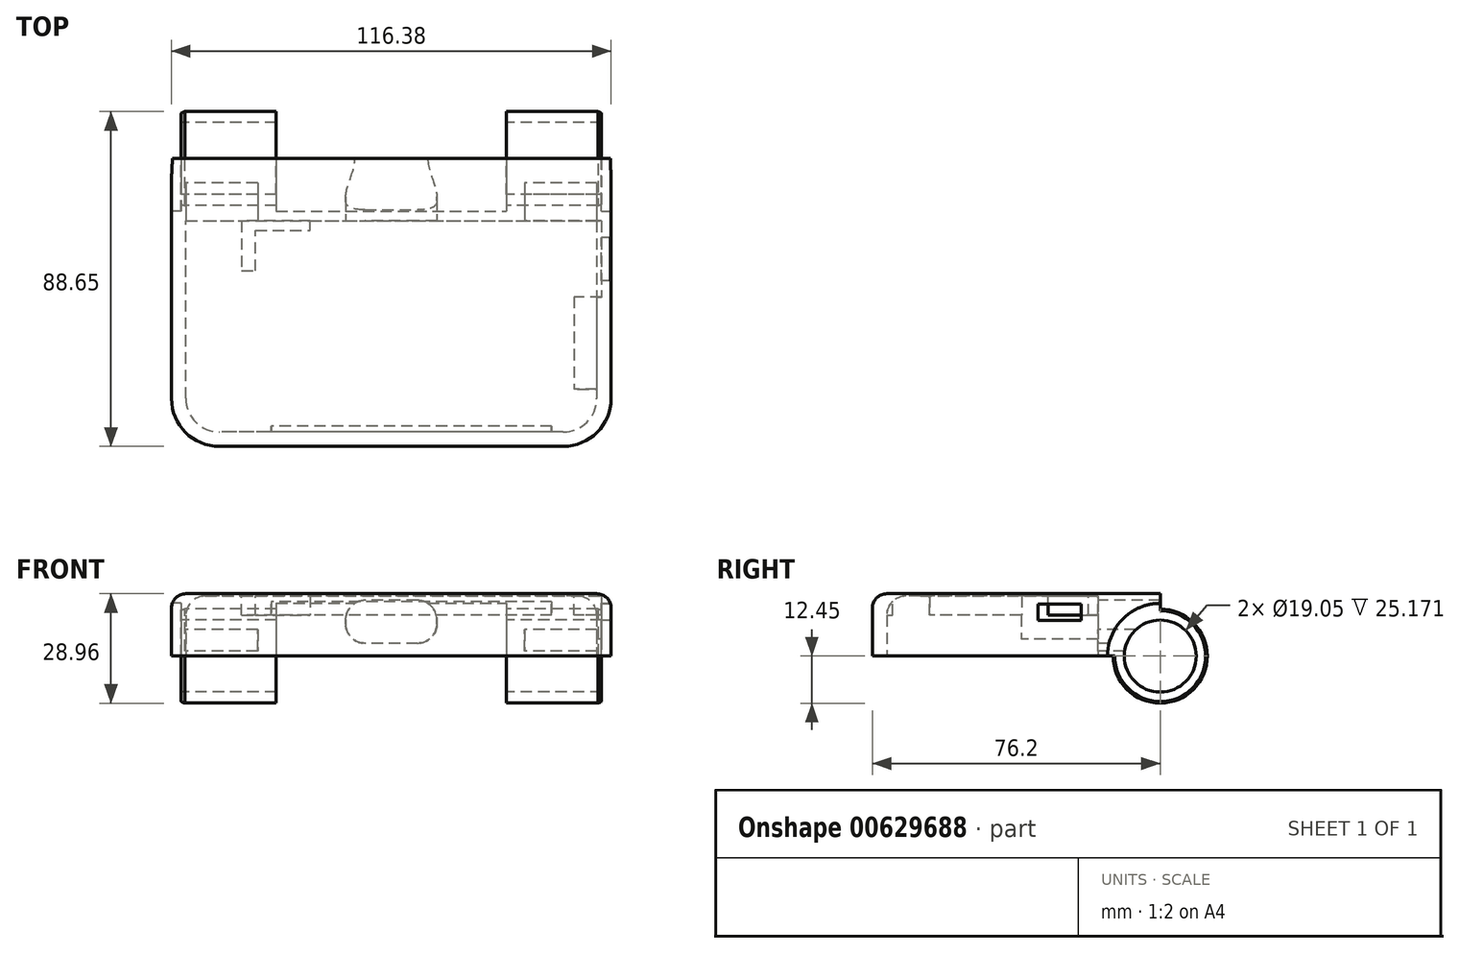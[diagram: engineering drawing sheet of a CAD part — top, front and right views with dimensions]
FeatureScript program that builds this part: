
annotation { "Feature Type Name" : "Feature", "Feature Type Description" : "" }
export const myFeature = defineFeature(function(context is Context, id is Id, definition is map)
    precondition{}
    {
        {
            var Q0;
            Q0=qCreatedBy(makeId("Top.planeOp"),FACE);
            var sketch = newSketch(context, id + "F0", { "sketchPlane" : qUnion([Q0])});
            skLineSegment(sketch, "E0.bottom", {"start": v(58.2, 38.1) * mm, "end": v(-58.2, 38.1) * mm});
            skLineSegment(sketch, "E0.top", {"start": v(58.2, -38.1) * mm, "end": v(-58.2, -38.1) * mm});
            skLineSegment(sketch, "E0.left", {"start": v(58.2, 38.1) * mm, "end": v(58.2, -38.1) * mm});
            skLineSegment(sketch, "E0.right", {"start": v(-58.2, 38.1) * mm, "end": v(-58.2, -38.1) * mm});
            skPoint(sketch, "E0.middle", {"position": v(0, 0) * mm});
            skSolve(sketch);
        }
        {
            var Q0;
            Q0 = qSketchRegion(id + "F0", true);
            extrude(context, id + "F1", {"entities" : qUnion([Q0]), "depth" : 16.5 * mm, "offsetDistance" : 25.4 * mm});
        }
        {
            var Q0;
            Q0=qCreatedBy(makeId("Right.planeOp"),FACE);
            var sketch = newSketch(context, id + "F2", { "sketchPlane" : qUnion([Q0])});
            skCircle(sketch, "E1", {"center": v(38.1, 0) * mm, "radius": 12.7 * mm});
            skSolve(sketch);
        }
        {
            var Q0;
            Q0 = qSketchRegion(id + "F2", true);
            extrude(context, id + "F3", {"entities" : qUnion([Q0]), "operationType" : NewBodyOperationType.ADD, "endBound" : BoundingType.SYMMETRIC, "depth" : 116.38 * mm, "offsetDistance" : 25.4 * mm});
        }
        {
            var Q0;
            Q0=makeQuery(id+"F1.opExtrude","SWEPT_EDGE",EDGE,{"disambiguationData":[OSD([sQuery(id+"F0.wireOp",EDGE,"E0.top"),sQuery(id+"F0.wireOp",EDGE,"E0.right")])]});
            var Q1;
            Q1=makeQuery(id+"F1.opExtrude","SWEPT_EDGE",EDGE,{"disambiguationData":[OSD([sQuery(id+"F0.wireOp",EDGE,"E0.top"),sQuery(id+"F0.wireOp",EDGE,"E0.left")])]});
            fillet(context, id + "F4", {"entities" : qUnion([Q0, Q1]), "radius" : 12.7 * mm, "tangentPropagation" : true, "allowEdgeOverflow" : false});
        }
        {
            var Q0;
            Q0=makeQuery(id+"F1.opExtrude","CAP_FACE",FACE,{"disambiguationData":[OSD([sQuery(id+"F0.wireOp",EDGE,"E0.bottom"),sQuery(id+"F0.wireOp",EDGE,"E0.top"),sQuery(id+"F0.wireOp",EDGE,"E0.left"),sQuery(id+"F0.wireOp",EDGE,"E0.right")])],"isStart":true});
            var sketch = newSketch(context, id + "F5", { "sketchPlane" : qUnion([Q0])});
            skLineSegment(sketch, "E2.0", {"start": v(-54.38, -21.6) * mm, "end": v(54.38, -21.6) * mm});
            skArc(sketch, "E2.1", {"start": v(54.38, 25.4) * mm, "mid": v(51.78, 31.69) * mm, "end": v(45.5, 34.29) * mm});
            skLineSegment(sketch, "E2.2", {"start": v(45.5, 34.3) * mm, "end": v(-45.5, 34.3) * mm});
            skLineSegment(sketch, "E2.3", {"start": v(54.38, -21.6) * mm, "end": v(54.38, 25.4) * mm});
            skArc(sketch, "E2.4", {"start": v(-45.5, 34.3) * mm, "mid": v(-51.78, 31.69) * mm, "end": v(-54.38, 25.4) * mm});
            skLineSegment(sketch, "E2.5", {"start": v(-54.38, 25.4) * mm, "end": v(-54.38, -21.6) * mm});
            skSolve(sketch);
        }
        {
            var Q0;
            Q0 = qSketchRegion(id + "F5", true);
            extrude(context, id + "F6", {"entities" : qUnion([Q0]), "operationType" : NewBodyOperationType.REMOVE, "oppositeDirection" : true, "depth" : 15.88 * mm, "offsetDistance" : 25.4 * mm});
        }
        {
            var Q0;
            Q0=qCreatedBy(makeId("Right.planeOp"),FACE);
            var sketch = newSketch(context, id + "F7", { "sketchPlane" : qUnion([Q0])});
            skCircle(sketch, "E3", {"center": v(38.1, 0) * mm, "radius": 6.99 * mm});
            skSolve(sketch);
        }
        {
            var Q0;
            Q0=qCreatedBy(makeId("Top.planeOp"),FACE);
            var sketch = newSketch(context, id + "F8", { "sketchPlane" : qUnion([Q0])});
            skLineSegment(sketch, "E4", {"start": v(0, 25.4) * mm, "end": v(-30.48, 25.4) * mm, "construction": true});
            skLineSegment(sketch, "E5", {"start": v(-30.48, 25.4) * mm, "end": v(-30.48, 28.58) * mm});
            skLineSegment(sketch, "E6", {"start": v(-30.48, 28.58) * mm, "end": v(-24.13, 28.58) * mm});
            skLineSegment(sketch, "E7", {"start": v(-24.13, 28.58) * mm, "end": v(-24.13, 28.58) * mm});
            skLineSegment(sketch, "E8", {"start": v(-24.13, 28.58) * mm, "end": v(-19.05, 28.58) * mm});
            skLineSegment(sketch, "E9", {"start": v(-19.05, 28.57) * mm, "end": v(-19.05, 38.1) * mm});
            skLineSegment(sketch, "E10", {"start": v(-19.05, 38.1) * mm, "end": v(0, 38.1) * mm});
            skLineSegment(sketch, "E11", {"start": v(0, 38.1) * mm, "end": v(19.05, 38.1) * mm});
            skLineSegment(sketch, "E12", {"start": v(19.05, 38.1) * mm, "end": v(19.05, 28.57) * mm});
            skLineSegment(sketch, "E13", {"start": v(19.05, 28.57) * mm, "end": v(24.13, 28.58) * mm});
            skLineSegment(sketch, "E14", {"start": v(24.13, 28.57) * mm, "end": v(24.13, 28.58) * mm});
            skLineSegment(sketch, "E15", {"start": v(24.13, 28.58) * mm, "end": v(30.48, 28.58) * mm});
            skLineSegment(sketch, "E16", {"start": v(30.48, 28.58) * mm, "end": v(30.48, 25.4) * mm});
            skLineSegment(sketch, "E17", {"start": v(30.48, 25.4) * mm, "end": v(0, 25.4) * mm, "construction": true});
            skLineSegment(sketch, "E18.0", {"start": v(-58.2, 50.8) * mm, "end": v(-58.2, 25.4) * mm});
            skLineSegment(sketch, "E19", {"start": v(-19.05, 38.1) * mm, "end": v(-58.2, 38.1) * mm, "construction": true});
            skLineSegment(sketch, "E20", {"start": v(-58.2, 25.4) * mm, "end": v(-30.48, 25.4) * mm, "construction": true});
            skLineSegment(sketch, "E21", {"start": v(-19.05, 28.58) * mm, "end": v(19.05, 28.58) * mm, "construction": true});
            skLineSegment(sketch, "E22", {"start": v(24.13, 28.58) * mm, "end": v(-24.13, 28.58) * mm, "construction": true});
            skLineSegment(sketch, "E23", {"start": v(-30.48, 25.4) * mm, "end": v(-30.48, 24.13) * mm});
            skLineSegment(sketch, "E24", {"start": v(-30.48, 24.13) * mm, "end": v(30.48, 24.13) * mm});
            skLineSegment(sketch, "E25", {"start": v(30.48, 24.13) * mm, "end": v(30.48, 25.4) * mm});
            skSolve(sketch);
        }
        {
            var Q0;
            Q0 = qSketchRegion(id + "F8", true);
            var Q1;
            Q1=sQuery(id+"F8.wireOp",EDGE,"E10");
            revolve(context, id + "F9", {"operationType" : NewBodyOperationType.REMOVE, "entities" : qUnion([Q0]), "axis" : qUnion([Q1]), "revolveType" : RevolveType.FULL, "oppositeDirection" : true});
        }
        {
            var Q0;
            Q0 = qSketchRegion(id + "F7", true);
            extrude(context, id + "F10", {"entities" : qUnion([Q0]), "operationType" : NewBodyOperationType.REMOVE, "depth" : 53.34 * mm, "offsetDistance" : 25.4 * mm, "hasSecondDirection" : true, "secondDirectionOppositeDirection" : true, "secondDirectionDepth" : 53.34 * mm});
        }
        {
            var Q0;
            Q0=makeQuery(id+"F6.boolean.opBoolean","COPY",FACE,{"derivedFrom":makeQuery(id+"F6.opExtrude","SWEPT_FACE",FACE,{"disambiguationData":[OSD([sQuery(id+"F5.wireOp",EDGE,"E2.0")])]})});
            var sketch = newSketch(context, id + "F11", { "sketchPlane" : qUnion([Q0])});
            skLineSegment(sketch, "E26.bottom", {"start": v(54.38, 1.27) * mm, "end": v(35.33, 1.27) * mm});
            skLineSegment(sketch, "E26.top", {"start": v(54.38, 6.98) * mm, "end": v(35.33, 6.98) * mm});
            skLineSegment(sketch, "E26.left", {"start": v(54.38, 1.27) * mm, "end": v(54.38, 6.98) * mm});
            skLineSegment(sketch, "E26.right", {"start": v(35.33, 1.27) * mm, "end": v(35.33, 6.98) * mm});
            skLineSegment(sketch, "E27.2", {"start": v(54.38, 15.88) * mm, "end": v(54.38, 0) * mm, "construction": true});
            skLineSegment(sketch, "E28.0", {"start": v(-54.38, 15.88) * mm, "end": v(-54.38, 0) * mm, "construction": true});
            skLineSegment(sketch, "E29.bottom", {"start": v(-54.38, 1.27) * mm, "end": v(-35.33, 1.27) * mm});
            skLineSegment(sketch, "E29.top", {"start": v(-54.38, 6.98) * mm, "end": v(-35.33, 6.98) * mm});
            skLineSegment(sketch, "E29.left", {"start": v(-54.38, 1.27) * mm, "end": v(-54.38, 6.98) * mm});
            skLineSegment(sketch, "E29.right", {"start": v(-35.33, 1.27) * mm, "end": v(-35.33, 6.98) * mm});
            skLineSegment(sketch, "E30", {"start": v(-35.33, 1.27) * mm, "end": v(35.33, 1.27) * mm, "construction": true});
            skSolve(sketch);
        }
        {
            var Q0;
            Q0 = qSketchRegion(id + "F11", true);
            extrude(context, id + "F12", {"entities" : qUnion([Q0]), "operationType" : NewBodyOperationType.REMOVE, "oppositeDirection" : true, "depth" : 17.78 * mm, "offsetDistance" : 25.4 * mm});
        }
        {
            var Q0;
            Q0=makeQuery(id+"F6.boolean.opBoolean","COPY",FACE,{"derivedFrom":makeQuery(id+"F6.opExtrude","SWEPT_FACE",FACE,{"disambiguationData":[OSD([sQuery(id+"F5.wireOp",EDGE,"E2.3")])]})});
            var sketch = newSketch(context, id + "F13", { "sketchPlane" : qUnion([Q0])});
            skLineSegment(sketch, "E31.bottom", {"start": v(-21.6, 15.88) * mm, "end": v(-1.27, 15.88) * mm});
            skLineSegment(sketch, "E31.top", {"start": v(-21.6, 4.44) * mm, "end": v(-1.27, 4.44) * mm});
            skLineSegment(sketch, "E31.left", {"start": v(-21.6, 15.88) * mm, "end": v(-21.6, 4.44) * mm});
            skLineSegment(sketch, "E31.right", {"start": v(-1.27, 15.88) * mm, "end": v(-1.27, 4.44) * mm});
            skSolve(sketch);
        }
        {
            var Q0;
            Q0 = qSketchRegion(id + "F13", true);
            extrude(context, id + "F14", {"entities" : qUnion([Q0]), "operationType" : NewBodyOperationType.REMOVE, "oppositeDirection" : true, "depth" : 1.27 * mm, "offsetDistance" : 25.4 * mm});
        }
        {
            var Q0;
            Q0=makeQuery(id+"F14.boolean.opBoolean","COPY",FACE,{"derivedFrom":makeQuery(id+"F14.opExtrude","CAP_FACE",FACE,{"disambiguationData":[OSD([sQuery(id+"F13.wireOp",EDGE,"E31.bottom"),sQuery(id+"F13.wireOp",EDGE,"E31.top"),sQuery(id+"F13.wireOp",EDGE,"E31.left"),sQuery(id+"F13.wireOp",EDGE,"E31.right")])],"isStart":false})});
            var sketch = newSketch(context, id + "F15", { "sketchPlane" : qUnion([Q0])});
            skLineSegment(sketch, "E32.top", {"start": v(-5.72, 9.42) * mm, "end": v(-17.15, 9.42) * mm});
            skLineSegment(sketch, "E32.left", {"start": v(-5.72, 13.8) * mm, "end": v(-5.72, 9.42) * mm});
            skLineSegment(sketch, "E32.right", {"start": v(-17.15, 13.8) * mm, "end": v(-17.15, 9.42) * mm});
            skLineSegment(sketch, "E33", {"start": v(-5.72, 13.8) * mm, "end": v(-11.43, 13.8) * mm});
            skLineSegment(sketch, "E34", {"start": v(-11.43, 13.8) * mm, "end": v(-17.15, 13.8) * mm});
            skLineSegment(sketch, "E35", {"start": v(-11.43, 15.88) * mm, "end": v(-11.43, 13.8) * mm, "construction": true});
            skSolve(sketch);
        }
        {
            var Q0;
            Q0 = qSketchRegion(id + "F15", true);
            extrude(context, id + "F16", {"entities" : qUnion([Q0]), "operationType" : NewBodyOperationType.REMOVE, "oppositeDirection" : true, "depth" : 25.4 * mm, "offsetDistance" : 25.4 * mm});
        }
        {
            var Q0;
            Q0=makeQuery(id+"F6.boolean.opBoolean","COPY",EDGE,{"derivedFrom":makeQuery(id+"F6.opExtrude","CAP_EDGE",EDGE,{"disambiguationData":[OSD([sQuery(id+"F5.wireOp",EDGE,"E2.5")])],"isStart":false})});
            fillet(context, id + "F17", {"entities" : qUnion([Q0]), "radius" : 5.08 * mm, "tangentPropagation" : true, "allowEdgeOverflow" : false});
        }
        {
            var Q0;
            Q0=makeQuery(id+"F14.boolean.opBoolean","MERGE",FACE,{"derivedFrom":[makeQuery(id+"F6.boolean.opBoolean","COPY",FACE,{"derivedFrom":makeQuery(id+"F6.opExtrude","CAP_FACE",FACE,{"disambiguationData":[OSD([sQuery(id+"F5.wireOp",EDGE,"E2.0"),sQuery(id+"F5.wireOp",EDGE,"E2.1"),sQuery(id+"F5.wireOp",EDGE,"E2.2"),sQuery(id+"F5.wireOp",EDGE,"E2.3"),sQuery(id+"F5.wireOp",EDGE,"E2.4"),sQuery(id+"F5.wireOp",EDGE,"E2.5")])],"isStart":false})}),makeQuery(id+"F14.opExtrude","SWEPT_FACE",FACE,{"disambiguationData":[OSD([sQuery(id+"F13.wireOp",EDGE,"E31.bottom")])]})]});
            var sketch = newSketch(context, id + "F18", { "sketchPlane" : qUnion([Q0])});
            skLineSegment(sketch, "E36.bottom", {"start": v(-33.43, -18.47) * mm, "end": v(48.06, -18.47) * mm, "construction": true});
            skLineSegment(sketch, "E36.top", {"start": v(-33.43, 32.5) * mm, "end": v(48.06, 32.5) * mm, "construction": true});
            skLineSegment(sketch, "E36.left", {"start": v(-33.43, -18.47) * mm, "end": v(-33.43, 32.5) * mm, "construction": true});
            skLineSegment(sketch, "E36.right", {"start": v(48.06, -18.47) * mm, "end": v(48.06, 32.5) * mm, "construction": true});
            skLineSegment(sketch, "E37.bottom", {"start": v(56.27, -1.48) * mm, "end": v(48.31, -1.48) * mm});
            skLineSegment(sketch, "E37.top", {"start": v(56.27, 22.88) * mm, "end": v(48.31, 22.88) * mm});
            skLineSegment(sketch, "E37.left", {"start": v(56.27, -1.48) * mm, "end": v(56.27, 22.88) * mm});
            skLineSegment(sketch, "E37.right", {"start": v(48.31, -1.48) * mm, "end": v(48.31, 22.88) * mm});
            skLineSegment(sketch, "E38", {"start": v(-35.97, -8.37) * mm, "end": v(-35.97, -19.1) * mm});
            skLineSegment(sketch, "E39", {"start": v(-35.97, -19.1) * mm, "end": v(-21.44, -19.1) * mm});
            skLineSegment(sketch, "E40", {"start": v(-21.44, -19.1) * mm, "end": v(-21.44, -22.38) * mm});
            skLineSegment(sketch, "E41", {"start": v(-21.44, -22.38) * mm, "end": v(-39.65, -22.38) * mm});
            skLineSegment(sketch, "E42", {"start": v(-39.65, -22.38) * mm, "end": v(-39.65, -8.37) * mm});
            skLineSegment(sketch, "E43", {"start": v(-39.65, -8.37) * mm, "end": v(-35.97, -8.37) * mm});
            skLineSegment(sketch, "E44.bottom", {"start": v(-31.77, 35.3) * mm, "end": v(42.42, 35.3) * mm});
            skLineSegment(sketch, "E44.top", {"start": v(-31.77, 32.75) * mm, "end": v(42.42, 32.75) * mm});
            skLineSegment(sketch, "E44.left", {"start": v(-31.77, 35.3) * mm, "end": v(-31.77, 32.75) * mm});
            skLineSegment(sketch, "E44.right", {"start": v(42.42, 35.3) * mm, "end": v(42.42, 32.75) * mm});
            skSolve(sketch);
        }
        {
            var Q0;
            Q0 = qSketchRegion(id + "F18", true);
            extrude(context, id + "F19", {"entities" : qUnion([Q0]), "operationType" : NewBodyOperationType.ADD, "depth" : 5.08 * mm, "offsetDistance" : 25.4 * mm});
        }
        {
            var Q0;
            Q0=makeQuery(id+"F1.opExtrude","CAP_EDGE",EDGE,{"disambiguationData":[OSD([sQuery(id+"F0.wireOp",EDGE,"E0.right")])],"isStart":false});
            fillet(context, id + "F20", {"entities" : qUnion([Q0]), "radius" : 3.8 * mm, "tangentPropagation" : true, "allowEdgeOverflow" : false});
        }
        {
            var Q0;
            Q0=makeQuery(id+"F3.opExtrude","CAP_EDGE",EDGE,{"disambiguationData":[OSD([sQuery(id+"F2.wireOp",EDGE,"E1")])],"isStart":false});
            var Q1;
            Q1=makeQuery(id+"F3.opExtrude","CAP_EDGE",EDGE,{"disambiguationData":[OSD([sQuery(id+"F2.wireOp",EDGE,"E1")])],"isStart":true});
            fillet(context, id + "F21", {"entities" : qUnion([Q0, Q1]), "radius" : 5.08 * mm, "tangentPropagation" : true, "allowEdgeOverflow" : false});
        }
        {
            var Q0;
            Q0=makeQuery(id+"F3.boolean.opBoolean","MERGE",FACE,{"derivedFrom":[makeQuery(id+"F1.opExtrude","SWEPT_FACE",FACE,{"disambiguationData":[OSD([sQuery(id+"F0.wireOp",EDGE,"E0.right")])]}),makeQuery(id+"F3.opExtrude","CAP_FACE",FACE,{"disambiguationData":[OSD([sQuery(id+"F2.wireOp",EDGE,"E1")])],"isStart":true})]});
            var sketch = newSketch(context, id + "F22", { "sketchPlane" : qUnion([Q0])});
            skCircle(sketch, "E45", {"center": v(-38.1, 0) * mm, "radius": 13.97 * mm});
            skSolve(sketch);
        }
        {
            var Q0;
            Q0 = qSketchRegion(id + "F22", true);
            extrude(context, id + "F23", {"entities" : qUnion([Q0]), "operationType" : NewBodyOperationType.REMOVE, "oppositeDirection" : true, "depth" : 2.54 * mm, "offsetDistance" : 25.4 * mm});
        }
        {
            var Q0;
            Q0=makeQuery(id+"F3.boolean.opBoolean","MERGE",FACE,{"derivedFrom":[makeQuery(id+"F1.opExtrude","SWEPT_FACE",FACE,{"disambiguationData":[OSD([sQuery(id+"F0.wireOp",EDGE,"E0.left")])]}),makeQuery(id+"F3.opExtrude","CAP_FACE",FACE,{"disambiguationData":[OSD([sQuery(id+"F2.wireOp",EDGE,"E1")])],"isStart":false})]});
            var sketch = newSketch(context, id + "F24", { "sketchPlane" : qUnion([Q0])});
            skCircle(sketch, "E46.0", {"center": v(38.1, 0) * mm, "radius": 13.97 * mm});
            skSolve(sketch);
        }
        {
            var Q0;
            Q0 = qSketchRegion(id + "F24", true);
            extrude(context, id + "F25", {"entities" : qUnion([Q0]), "operationType" : NewBodyOperationType.REMOVE, "oppositeDirection" : true, "depth" : 2.54 * mm, "offsetDistance" : 25.4 * mm});
        }
        {
            var Q0;
            Q0=qCreatedBy(makeId("Right.planeOp"),FACE);
            var sketch = newSketch(context, id + "F26", { "sketchPlane" : qUnion([Q0])});
            skCircle(sketch, "E47.0", {"center": v(38.1, 0) * mm, "radius": 9.52 * mm});
            skSolve(sketch);
        }
        {
            var Q0;
            Q0 = qSketchRegion(id + "F26", true);
            extrude(context, id + "F27", {"entities" : qUnion([Q0]), "operationType" : NewBodyOperationType.REMOVE, "endBound" : BoundingType.SYMMETRIC, "depth" : 127 * mm, "offsetDistance" : 25.4 * mm});
        }
        {
            var Q0;
            Q0=makeQuery(id+"F14.boolean.opBoolean","MERGE",FACE,{"derivedFrom":[makeQuery(id+"F6.boolean.opBoolean","COPY",FACE,{"derivedFrom":makeQuery(id+"F6.opExtrude","SWEPT_FACE",FACE,{"disambiguationData":[OSD([sQuery(id+"F5.wireOp",EDGE,"E2.0")])]})}),makeQuery(id+"F14.opExtrude","SWEPT_FACE",FACE,{"disambiguationData":[OSD([sQuery(id+"F13.wireOp",EDGE,"E31.left")])]})]});
            var sketch = newSketch(context, id + "F28", { "sketchPlane" : qUnion([Q0])});
            skLineSegment(sketch, "E48.bottom", {"start": v(6.99, 14.74) * mm, "end": v(-6.99, 14.74) * mm});
            skLineSegment(sketch, "E48.top", {"start": v(6.98, 3.42) * mm, "end": v(-6.98, 3.42) * mm});
            skLineSegment(sketch, "E48.left", {"start": v(12.07, 9.66) * mm, "end": v(12.07, 8.5) * mm});
            skLineSegment(sketch, "E48.right", {"start": v(-12.07, 9.66) * mm, "end": v(-12.07, 8.5) * mm});
            skPoint(sketch, "E49.visualSharp", {"position": v(12.07, 3.42) * mm});
            skArc(sketch, "E49.filletArc", {"start": v(6.98, 3.42) * mm, "mid": v(10.58, 4.9) * mm, "end": v(12.07, 8.5) * mm});
            skPoint(sketch, "E50.visualSharp", {"position": v(-12.07, 3.42) * mm});
            skArc(sketch, "E50.filletArc", {"start": v(-12.06, 8.5) * mm, "mid": v(-10.58, 4.9) * mm, "end": v(-6.99, 3.42) * mm});
            skPoint(sketch, "E51.visualSharp", {"position": v(-12.06, 14.74) * mm});
            skArc(sketch, "E51.filletArc", {"start": v(-6.99, 14.74) * mm, "mid": v(-10.58, 13.25) * mm, "end": v(-12.07, 9.66) * mm});
            skPoint(sketch, "E52.visualSharp", {"position": v(12.06, 14.74) * mm});
            skArc(sketch, "E52.filletArc", {"start": v(12.06, 9.66) * mm, "mid": v(10.58, 13.25) * mm, "end": v(6.99, 14.74) * mm});
            skLineSegment(sketch, "E53.0", {"start": v(-54.38, 0) * mm, "end": v(54.38, 0) * mm, "construction": true});
            skLineSegment(sketch, "E54", {"start": v(0, 0) * mm, "end": v(0, 14.74) * mm, "construction": true});
            skSolve(sketch);
        }
        {
            var Q0;
            Q0 = qSketchRegion(id + "F28", true);
            extrude(context, id + "F29", {"entities" : qUnion([Q0]), "operationType" : NewBodyOperationType.REMOVE, "oppositeDirection" : true, "depth" : 25.4 * mm, "offsetDistance" : 25.4 * mm});
        }
        {
            var Q0;
            Q0=qCreatedBy(makeId("Right.planeOp"),FACE);
            var sketch = newSketch(context, id + "F30", { "sketchPlane" : qUnion([Q0])});
            skArc(sketch, "E55", {"start": v(25.65, 0) * mm, "mid": v(46.9, -8.8) * mm, "end": v(38.1, 12.45) * mm});
            skLineSegment(sketch, "E56", {"start": v(25.65, 0) * mm, "end": v(20.57, 0) * mm});
            skLineSegment(sketch, "E57", {"start": v(20.57, 0) * mm, "end": v(20.57, -20.57) * mm});
            skLineSegment(sketch, "E58", {"start": v(20.57, -20.57) * mm, "end": v(58.67, -20.57) * mm});
            skLineSegment(sketch, "E59", {"start": v(58.67, -20.57) * mm, "end": v(58.67, 17.53) * mm});
            skLineSegment(sketch, "E60", {"start": v(58.67, 17.53) * mm, "end": v(38.1, 17.53) * mm});
            skLineSegment(sketch, "E61", {"start": v(38.1, 17.53) * mm, "end": v(38.1, 12.45) * mm});
            skSolve(sketch);
        }
        {
            var Q0;
            Q0 = qSketchRegion(id + "F30", true);
            extrude(context, id + "F31", {"entities" : qUnion([Q0]), "operationType" : NewBodyOperationType.REMOVE, "endBound" : BoundingType.SYMMETRIC, "depth" : 127 * mm, "offsetDistance" : 25.4 * mm});
        }
    });
